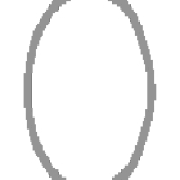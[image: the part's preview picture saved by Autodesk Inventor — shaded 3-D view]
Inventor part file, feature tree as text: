
AUTODESK INVENTOR PART (.ipt)
format: ipt  version: 2021 (Build 250183000, 183)  size: 111,616 bytes
history: native  units: in
note: dims shown in document units (in); Inventor stores cm internally (conversion verified against a paired STEP export)
features: other x4, sketch x3, plane x1
ambient origin geometry x8: Origin, YZ Plane, XZ Plane, XY Plane, X Axis, Y Axis, Z Axis, Center Point
bodies: Solid1 (feature_tree), Body (feature_tree)
feature tree (8):
  other  "Driven Length"
  other  "Frame Generator"
  other  "Start Plane"
  other  "End Plane"
  sketch  "Sketch"  dims[d2=13.0in d4=-0.0in d5=13.0in d6=0.12in d7=0.0in d16=90.0deg d9=13.0in]
  sketch  "Sketch10"  dims[d0=1.0in]
  plane  "Work Plane7"
  sketch  "Sketch11"  dims[d1=0.049in]
